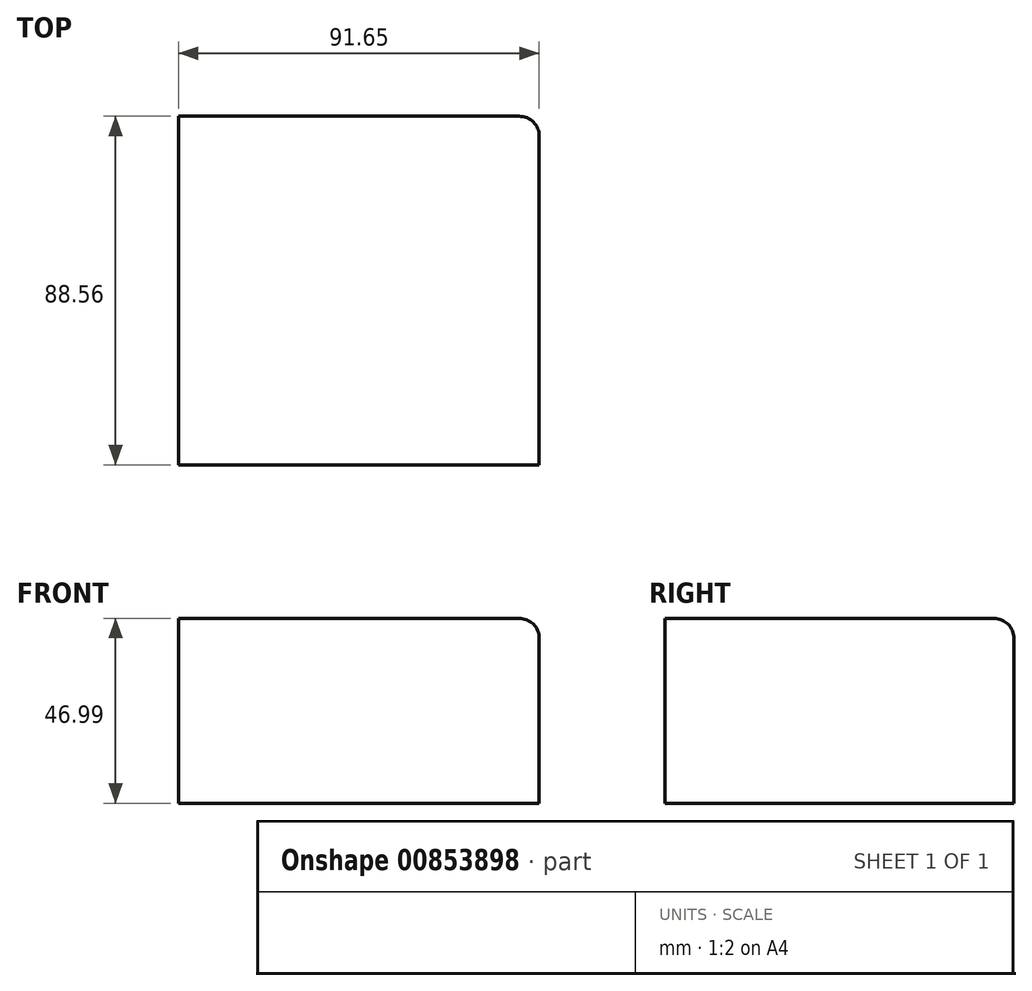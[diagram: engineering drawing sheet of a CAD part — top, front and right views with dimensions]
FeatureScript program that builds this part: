
annotation { "Feature Type Name" : "Feature", "Feature Type Description" : "" }
export const myFeature = defineFeature(function(context is Context, id is Id, definition is map)
    precondition{}
    {
        {
            var Q0;
            Q0=qCreatedBy(makeId("Top.planeOp"),FACE);
            var sketch = newSketch(context, id + "F0", { "sketchPlane" : qUnion([Q0])});
            skLineSegment(sketch, "E0.bottom", {"start": v(-49.98, 49.74) * mm, "end": v(41.67, 49.74) * mm});
            skLineSegment(sketch, "E0.top", {"start": v(-49.98, -38.82) * mm, "end": v(41.67, -38.82) * mm});
            skLineSegment(sketch, "E0.left", {"start": v(-49.98, 49.74) * mm, "end": v(-49.98, -38.82) * mm});
            skLineSegment(sketch, "E0.right", {"start": v(41.67, 49.74) * mm, "end": v(41.67, -38.82) * mm});
            skSolve(sketch);
        }
        {
            var Q0;
            Q0=makeQuery(id+"F0.imprint","IMPRINT",FACE,{"disambiguationData":[TD([[makeQuery(id+"F0.imprint","IMPRINT",EDGE,{"derivedFrom":sQuery(id+"F0.wireOp",EDGE,"E0.bottom")}),-1.0]])]});
            extrude(context, id + "F1", {"entities" : qUnion([Q0]), "depth" : 47 * mm, "offsetDistance" : 25.4 * mm});
        }
        {
            var Q0;
            Q0=makeQuery(id+"F1.opExtrude","CAP_EDGE",EDGE,{"disambiguationData":[OSD([sQuery(id+"F0.wireOp",EDGE,"E0.bottom")])],"isStart":false});
            var Q1;
            Q1=makeQuery(id+"F1.opExtrude","SWEPT_EDGE",EDGE,{"disambiguationData":[OSD([sQuery(id+"F0.wireOp",EDGE,"E0.bottom"),sQuery(id+"F0.wireOp",EDGE,"E0.right")])]});
            var Q2;
            Q2=makeQuery(id+"F1.opExtrude","CAP_EDGE",EDGE,{"disambiguationData":[OSD([sQuery(id+"F0.wireOp",EDGE,"E0.right")])],"isStart":false});
            fillet(context, id + "F2", {"entities" : qUnion([Q0, Q1, Q2]), "radius" : 5.08 * mm, "tangentPropagation" : true, "allowEdgeOverflow" : false});
        }
    });
